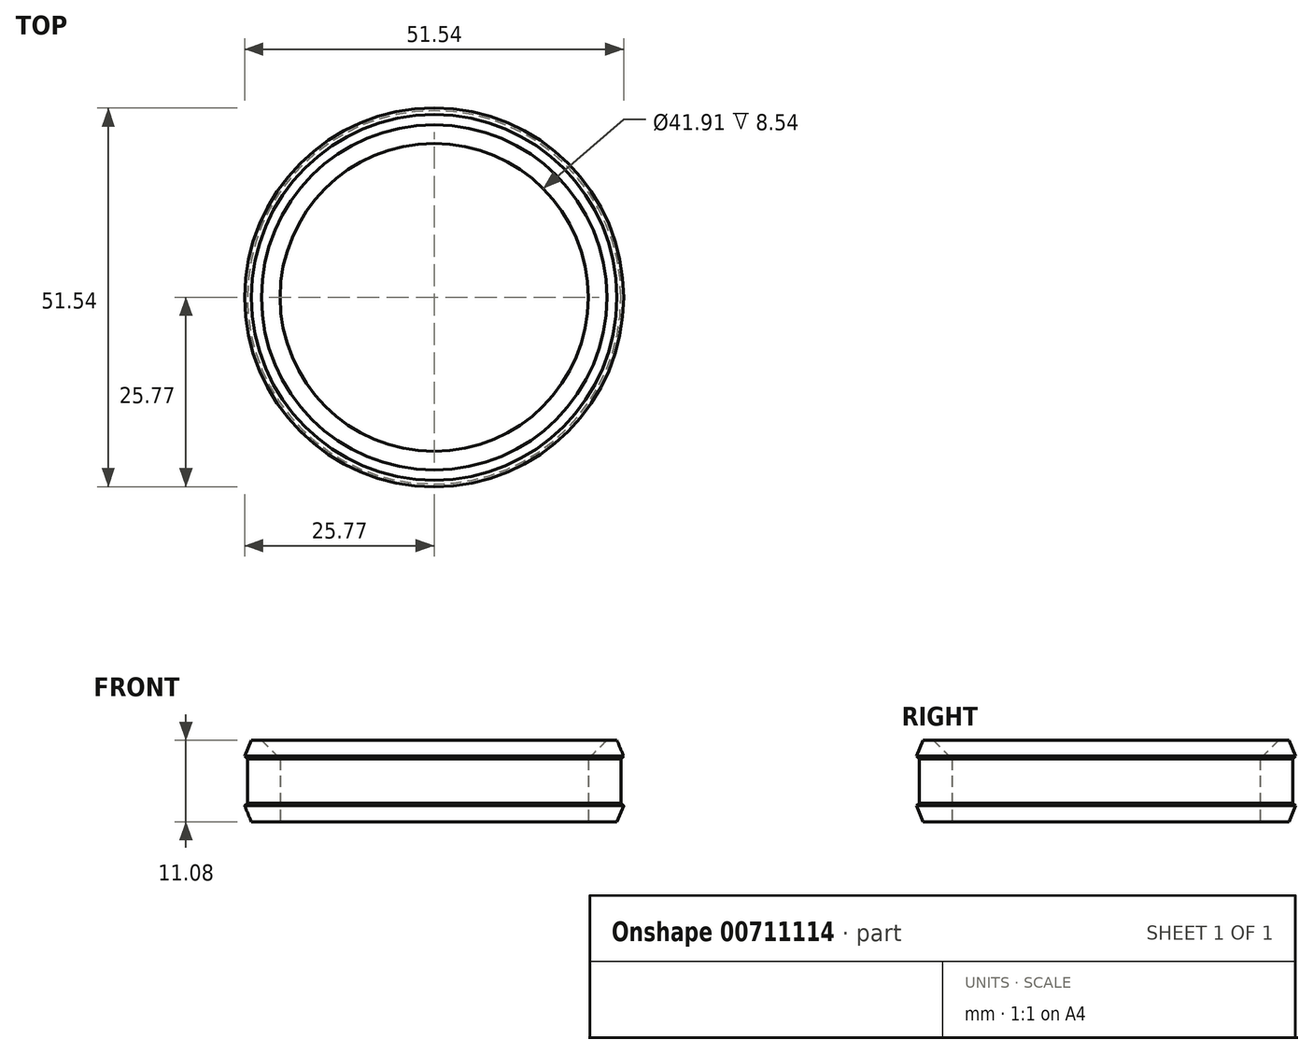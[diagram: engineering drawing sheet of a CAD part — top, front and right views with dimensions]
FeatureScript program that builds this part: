
annotation { "Feature Type Name" : "Feature", "Feature Type Description" : "" }
export const myFeature = defineFeature(function(context is Context, id is Id, definition is map)
    precondition{}
    {
        {
            var Q0;
            Q0=qCreatedBy(makeId("Top.planeOp"),FACE);
            var sketch = newSketch(context, id + "F0", { "sketchPlane" : qUnion([Q0])});
            skCircle(sketch, "E0", {"center": v(0, 0) * mm, "radius": 25.4 * mm});
            skSolve(sketch);
        }
        {
            var Q0;
            Q0=makeQuery(id+"F0.imprint","IMPRINT",FACE,{"disambiguationData":[TD([[makeQuery(id+"F0.imprint","IMPRINT",EDGE,{"derivedFrom":sQuery(id+"F0.wireOp",EDGE,"E0")}),1.0]])]});
            extrude(context, id + "F1", {"entities" : qUnion([Q0]), "depth" : 3 * mm, "offsetDistance" : 25.4 * mm});
        }
        {
            var Q0;
            Q0=makeQuery(id+"F1.opExtrude","CAP_FACE",FACE,{"disambiguationData":[OSD([sQuery(id+"F0.wireOp",EDGE,"E0")])],"isStart":false});
            extrude(context, id + "F2", {"entities" : qUnion([Q0]), "operationType" : NewBodyOperationType.ADD, "depth" : 2.54 * mm, "offsetDistance" : 25.4 * mm, "hasDraft" : true, "draftAngle" : 45 * degree});
        }
        {
            var Q0;
            Q0=makeQuery(id+"F1.opExtrude","SWEPT_BODY",BODY,{"disambiguationData":[OSD([sQuery(id+"F0.wireOp",EDGE,"E0")])]});
            var Q1;
            Q1=qCreatedBy(makeId("Top.planeOp"),FACE);
            mirror(context, id + "F3", {"operationType" : NewBodyOperationType.ADD, "entities" : qUnion([Q0]), "mirrorPlane" : qUnion([Q1])});
        }
        {
            var Q0;
            Q0=makeQuery(id+"F2.opExtrude","CAP_EDGE",EDGE,{"disambiguationData":[OSD([sQuery(id+"F0.wireOp",EDGE,"E0")])],"isStart":false});
            var Q1;
            Q1=makeQuery(id+"F3.opPattern","COPY",EDGE,{"derivedFrom":makeQuery(id+"F2.opExtrude","CAP_EDGE",EDGE,{"disambiguationData":[OSD([sQuery(id+"F0.wireOp",EDGE,"E0")])],"isStart":false}),"instanceName":"1"});
            chamfer(context, id + "F4", {"entities" : qUnion([Q0, Q1]), "width" : 1.27 * mm, "tangentPropagation" : true});
        }
        {
            var Q0;
            Q0=makeQuery(id+"F3.opPattern","COPY",FACE,{"derivedFrom":makeQuery(id+"F2.opExtrude","CAP_FACE",FACE,{"disambiguationData":[OSD([sQuery(id+"F0.wireOp",EDGE,"E0")])],"isStart":false}),"instanceName":"1"});
            var sketch = newSketch(context, id + "F5", { "sketchPlane" : qUnion([Q0])});
            skCircle(sketch, "E1", {"center": v(0, 0) * mm, "radius": 20.96 * mm});
            skSolve(sketch);
        }
        {
            var Q0;
            Q0=makeQuery(id+"F5.imprint","IMPRINT",FACE,{"disambiguationData":[TD([[makeQuery(id+"F5.imprint","IMPRINT",EDGE,{"derivedFrom":sQuery(id+"F5.wireOp",EDGE,"E1")}),1.0]])]});
            extrude(context, id + "F6", {"entities" : qUnion([Q0]), "operationType" : NewBodyOperationType.REMOVE, "endBound" : BoundingType.THROUGH_ALL, "oppositeDirection" : true, "depth" : 40.64 * mm, "offsetDistance" : 25.4 * mm});
        }
        {
            var Q0;
            Q0=makeQuery(id+"F6.boolean.opBoolean","INTERSECT",EDGE,{"derivedFrom":[makeQuery(id+"F2.opExtrude","CAP_FACE",FACE,{"disambiguationData":[OSD([sQuery(id+"F0.wireOp",EDGE,"E0")])],"isStart":false}),makeQuery(id+"F6.opExtrude","SWEPT_FACE",FACE,{"disambiguationData":[OSD([sQuery(id+"F5.wireOp",EDGE,"E1")])]})]});
            var Q1;
            Q1=makeQuery(id+"F6.boolean.opBoolean","COPY",EDGE,{"derivedFrom":makeQuery(id+"F6.opExtrude","CAP_EDGE",EDGE,{"disambiguationData":[OSD([sQuery(id+"F5.wireOp",EDGE,"E1")])],"isStart":true})});
            chamfer(context, id + "F7", {"entities" : qUnion([Q0, Q1]), "width" : 2.54 * mm, "tangentPropagation" : true});
        }
    });
